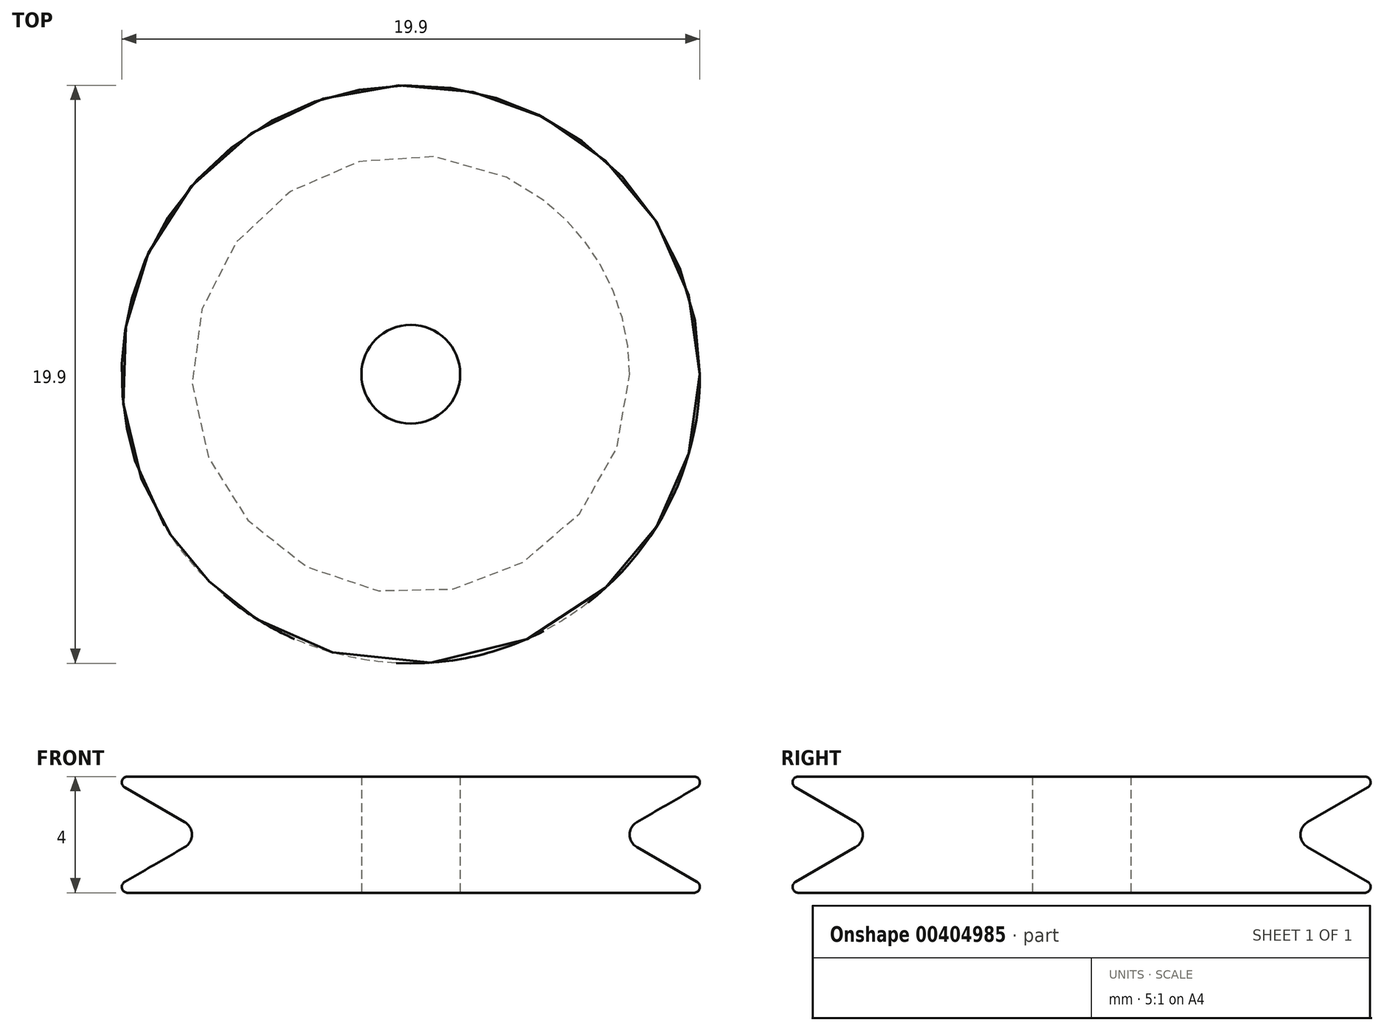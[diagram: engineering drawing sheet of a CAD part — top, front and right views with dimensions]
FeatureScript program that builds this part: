
annotation { "Feature Type Name" : "Feature", "Feature Type Description" : "" }
export const myFeature = defineFeature(function(context is Context, id is Id, definition is map)
    precondition{}
    {
        {
            var Q0;
            Q0=qCreatedBy(makeId("Top.planeOp"),FACE);
            var sketch = newSketch(context, id + "F0", { "sketchPlane" : qUnion([Q0])});
            skCircle(sketch, "E0", {"center": v(0, 0) * mm, "radius": 1.7 * mm});
            skCircle(sketch, "E1", {"center": v(0, 0) * mm, "radius": 10.5 * mm});
            skSolve(sketch);
        }
        {
            var Q0;
            Q0=makeQuery(id+"F0.imprint","IMPRINT",FACE,{"disambiguationData":[TD([[makeQuery(id+"F0.imprint","IMPRINT",EDGE,{"derivedFrom":sQuery(id+"F0.wireOp",EDGE,"E0")}),-1.0]])]});
            extrude(context, id + "F1", {"entities" : qUnion([Q0]), "depth" : 4 * mm});
        }
        {
            var Q0;
            Q0=qCreatedBy(makeId("Front.planeOp"),FACE);
            var sketch = newSketch(context, id + "F2", { "sketchPlane" : qUnion([Q0])});
            skLineSegment(sketch, "E2", {"start": v(-10.5, 0) * mm, "end": v(-7.04, 2) * mm});
            skLineSegment(sketch, "E3", {"start": v(-7.04, 2) * mm, "end": v(-10.5, 4) * mm});
            skLineSegment(sketch, "E4", {"start": v(-10.5, 0) * mm, "end": v(-10.5, 4) * mm});
            skLineSegment(sketch, "E5", {"start": v(-10.5, 0) * mm, "end": v(0, 0) * mm});
            skSolve(sketch);
        }
        {
            var Q0;
            Q0=qSketchRegion(id+"F2",true);
            var Q1;
            Q1=makeQuery(id+"F1.opExtrude","CAP_EDGE",EDGE,{"disambiguationData":[OSD([sQuery(id+"F0.wireOp",EDGE,"E1")])],"isStart":false});
            revolve(context, id + "F3", {"operationType" : NewBodyOperationType.REMOVE, "entities" : qUnion([Q0]), "axis" : qUnion([Q1]), "revolveType" : RevolveType.FULL, "oppositeDirection" : true});
        }
        {
            var Q0;
            Q0=makeQuery(id+"F3.boolean.opBoolean","MERGE",EDGE,{"derivedFrom":[makeQuery(id+"F1.opExtrude","CAP_EDGE",EDGE,{"disambiguationData":[OSD([sQuery(id+"F0.wireOp",EDGE,"E1")])],"isStart":false}),makeQuery(id+"F3.opRevolve","SWEPT_EDGE",EDGE,{"disambiguationData":[OSD([sQuery(id+"F2.wireOp",EDGE,"E3"),sQuery(id+"F2.wireOp",EDGE,"E4")])]})]});
            var Q1;
            Q1=makeQuery(id+"F3.boolean.opBoolean","MERGE",EDGE,{"derivedFrom":[makeQuery(id+"F1.opExtrude","CAP_EDGE",EDGE,{"disambiguationData":[OSD([sQuery(id+"F0.wireOp",EDGE,"E1")])],"isStart":true}),makeQuery(id+"F3.opRevolve","SWEPT_EDGE",EDGE,{"disambiguationData":[OSD([sQuery(id+"F2.wireOp",EDGE,"E2"),sQuery(id+"F2.wireOp",EDGE,"E4")])]})]});
            fillet(context, id + "F4", {"entities" : qUnion([Q0, Q1]), "radius" : .2 * mm, "tangentPropagation" : true, "allowEdgeOverflow" : false});
        }
        {
            var Q0;
            Q0=makeQuery(id+"F3.boolean.opBoolean","COPY",EDGE,{"derivedFrom":makeQuery(id+"F3.opRevolve","SWEPT_EDGE",EDGE,{"disambiguationData":[OSD([sQuery(id+"F2.wireOp",EDGE,"E2"),sQuery(id+"F2.wireOp",EDGE,"E3")])]})});
            fillet(context, id + "F5", {"entities" : qUnion([Q0]), "radius" : .5 * mm, "tangentPropagation" : true, "allowEdgeOverflow" : false});
        }
    });
